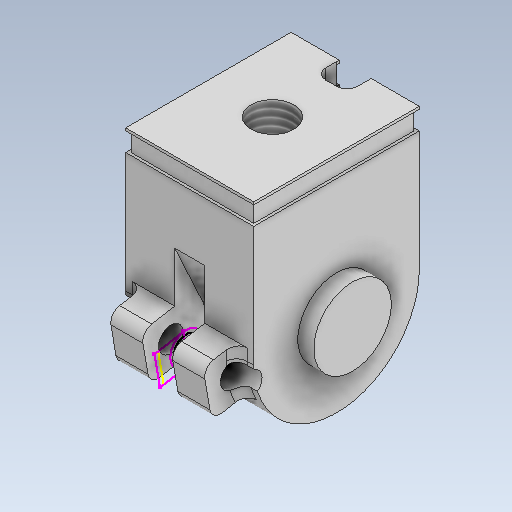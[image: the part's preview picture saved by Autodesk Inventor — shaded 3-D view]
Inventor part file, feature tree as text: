
AUTODESK INVENTOR PART (.ipt)
format: ipt  version: 2021 (Build 250183000, 183)  size: 532,480 bytes
history: native  units: mm
features: sketch x21, extrude x14, plane x7, other x4, fillet x4, hole x2, thread x2, revolve x1, shell x1, sweep x1
ambient origin geometry x8: Origin, YZ Plane, XZ Plane, XY Plane, X Axis, Y Axis, Z Axis, Center Point
bodies: Body1 (feature_tree)
feature tree (57):
  other  "Sólido1"
  revolve  "Revolución1"  [1 undecoded]
  shell  "Vaciado1"  Thickness=90.0deg
  extrude  "Extrusión1"  Depth=10.0mm
  extrude  "Extrusión2"  TaperAngle=0.0deg  [1 undecoded]
  sketch  "Boceto4"  dims[d16=2.0mm d17=8.0mm]
  plane  "Plano de trabajo4"
  sketch  "Boceto6"  dims[d20=8.0mm d22=20.0mm]
  plane  "Plano de trabajo1"
  sketch  "Boceto7"  dims[d23=5.0mm d24=0.0mm d25=12.0mm]
  sweep  "Barrido2"
  extrude  "Extrusión5"  Depth=20.0mm
  extrude  "Extrusión6"  Depth=12.0mm
  plane  "Plano de trabajo2"
  sketch  "Boceto12"  dims[d57=18.0mm d60=10.0mm]
  extrude  "Extrusión8"  Depth=4.0mm
  fillet  "Empalme3"  Radius=2.0mm
  extrude  "Extrusión9"  Depth=2.0mm
  extrude  "Extrusión10"  Depth=26.0mm
  plane  "Plano de trabajo3"
  extrude  "Extrusión11"  Depth=10.0mm
  hole  "Agujero1"  [1 undecoded]
  plane  "Plano de trabajo5"
  plane  "Plano de trabajo6"
  extrude  "Extrusión12"  Depth=0.5mm
  hole  "Agujero2"  [1 undecoded]
  thread  "Rosca2"  [1 undecoded]
  thread  "Rosca3"  [1 undecoded]
  extrude  "Extrusión14"  Depth=7.25mm
  fillet  "Empalme4"  Radius=11.25mm
  sketch  "Boceto23"  dims[d100=34.0mm d103=8.5mm d104=25.0mm d106=20.0mm]
  plane  "Plano de trabajo7"
  extrude  "Extrusión17"  TaperAngle=0.0deg  [1 undecoded]
  extrude  "Extrusión18"  Depth=9.5mm
  extrude  "Extrusión19"  Depth=0.5mm
  extrude  "Extrusión20"  Depth=8.5mm
  fillet  "Empalme5"  Radius=25.0mm
  fillet  "Empalme6"  Radius=20.0mm
  sketch  "Boceto1"  dims[d1=0.0mm d3=34.0mm d4=90.0deg]
  sketch  "Boceto3"  dims[d13=40.0mm d14=0.0mm]
  sketch  "Boceto 3D1"  dims[d7=10.0mm d12=2.0mm]
  other  "Intersección 3D1"
  sketch  "Boceto8"  dims[d26=5.0mm d34=4.0mm d35=2.0mm]
  sketch  "Boceto9"  dims[d36=1.5mm d46=2.0mm d48=8.0mm d49=8.0mm]
  sketch  "Boceto10"  dims[d55=9.0mm d56=26.0mm]
  other  "Intersección 3D4"
  other  "Intersección 3D6"
  sketch  "Boceto13"  dims[d61=26.0mm d70=2.0mm]
  sketch  "Boceto14"  dims[d71=1.0mm d72=0.5mm]
  sketch  "Boceto15"  dims[d73=0.5mm d78=0.0mm d79=0.0mm d82=7.75mm d84=12.0mm]
  sketch  "Boceto16"  dims[d85=0.0mm d86=7.25mm d87=11.25mm]
  sketch  "Boceto17"  dims[d88=15.0mm d89=0.0mm]
  sketch  "Boceto18"  dims[d94=8.5mm d95=9.5mm]
  sketch  "Boceto21"  dims[d98=0.5mm d99=0.5mm]
  sketch  "Boceto24"  dims[d107=32.599342mm]
  sketch  "Boceto25"  dims[d115=11.25mm]
  sketch  "Boceto26"  dims[d116=0.0mm d117=11.25mm d118=8.25mm d119=29.697249mm d120=2.3mm d121=11.25mm d122=8.25mm d123=29.697249mm d124=2.8mm d125=2.4mm d126=2.4mm d127=2.4mm d128=8.8mm d129=0.0mm d130=1.0mm d131=6.6mm d132=3.3mm d133=3.0mm d134=6.6mm d135=2.8mm d136=0.0mm d137=15.0deg d138=1.5mm d139=16.0mm d140=1.5mm d141=1.0mm d143=3.0mm d144=3.0mm d145=3.0mm d146=3.0mm d147=6.0mm d148=0.0mm d149=10.0mm d150=9.0mm d151=4.0mm d152=0.5mm d153=0.0mm d154=2.0mm d155=2.0mm d156=6.0mm d157=4.0mm d158=2.0mm d159=90.0deg d160=8.0mm d161=0.0mm d162=-3.0mm d163=19.0mm d164=8.0mm d165=6.0mm d166=0.0mm d167=8.0mm d168=4.0mm d169=6.0mm d170=8.0mm d171=2.0mm d172=90.0deg d173=20.0mm d174=0.0mm d175=19.0mm d176=0.0mm d177=7.0mm d178=0.0mm d185=11.25mm d186=8.25mm d187=29.697249mm d188=2.3mm d189=4.3mm d190=0.0mm d191=1.0mm d201=11.25mm d202=8.25mm d203=29.697249mm d204=2.3mm d205=2.4mm d206=2.4mm d209=-2.0mm d210=60.0mm d211=60.0mm d212=84.0mm d213=0.0mm d214=11.5mm d215=15.0mm d216=60.0mm d217=60.0mm d218=2.0mm d219=0.0mm d220=12.0mm d221=15.5mm d222=0.25mm d223=0.0mm d224=5.0mm d226=3.0mm d227=3.0mm d228=1.0mm d229=8.0mm d230=0.0mm d231=4.0mm d232=4.0mm d234=7.0mm d235=1.5mm d236=0.0mm d237=1.5mm]
note: 7 required parameter values undecoded (feature->parameter linkage not recoverable at this tier; creation-order binding heuristic only, values carry confidence <= 0.55)